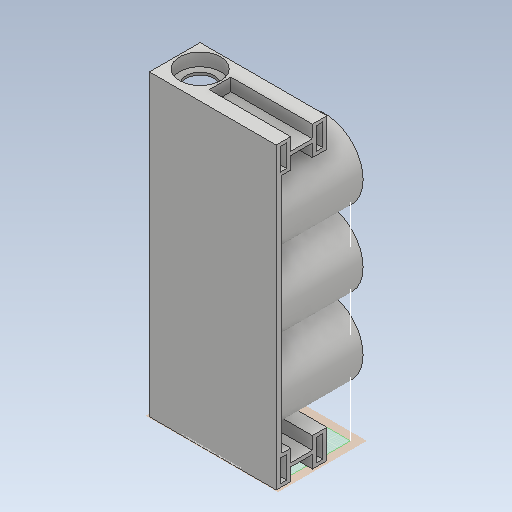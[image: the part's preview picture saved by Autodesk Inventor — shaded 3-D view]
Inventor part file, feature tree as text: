
AUTODESK INVENTOR PART (.ipt)
format: ipt  version: 2020 (Build 240168000, 168)  size: 757,760 bytes
history: native  units: mm
features: sketch x25, extrude x22, fillet x4
ambient origin geometry x8: Origin, YZ Plane, XZ Plane, XY Plane, X Axis, Y Axis, Z Axis, Center Point
bodies: Solid1 (feature_tree)
feature tree (51):
  extrude  "Extrusion1"  Depth=165.0mm
  extrude  "Extrusion2"  Depth=8.5mm
  extrude  "Extrusion3"  Depth=25.0mm TaperAngle=0.0deg
  extrude  "Extrusion4"  Depth=22.75mm
  extrude  "Extrusion5"  Depth=15.5mm
  extrude  "Extrusion6"  Depth=7.1mm TaperAngle=0.0deg
  fillet  "Fillet1"  Radius=5.0mm
  extrude  "Extrusion7"  Depth=10.0mm TaperAngle=0.0deg
  fillet  "Fillet2"  Radius=2.0mm
  extrude  "Extrusion8"  Depth=16.0mm
  extrude  "Extrusion9"  Depth=16.0mm
  fillet  "Fillet3"  Radius=8.0mm
  extrude  "Extrusion10"  Depth=6.0mm
  extrude  "Extrusion11"  Depth=12.25mm
  sketch  "Sketch12"  dims[d32=12.25mm d33=3.5mm]
  sketch  "Sketch13"  dims[d34=12.25mm d35=12.25mm]
  extrude  "Extrusion12"  Depth=12.25mm
  extrude  "Extrusion13"  Depth=12.25mm
  sketch  "Sketch16"  dims[d41=8.0mm d42=1.0mm]
  extrude  "Extrusion14"  Depth=40.0mm TaperAngle=0.0deg
  extrude  "Extrusion15"  Depth=2.0mm
  extrude  "Extrusion16"  Depth=1.0mm
  extrude  "Extrusion17"  Depth=2.0mm TaperAngle=0.0deg
  extrude  "Extrusion18"  Depth=7.1mm TaperAngle=0.0deg
  fillet  "Fillet4"  Radius=3.0mm
  extrude  "Extrusion19"  Depth=42.0mm
  extrude  "Extrusion20"  Depth=42.0mm
  extrude  "Extrusion21"  Depth=42.0mm
  extrude  "Extrusion22"  Depth=2.0mm
  sketch  "Sketch1"  dims[d0=25.0mm d1=165.0mm]
  sketch  "Sketch2"  dims[d2=3.0mm d3=0.0mm d4=8.5mm]
  sketch  "Sketch3"  dims[d5=8.5mm d6=25.0mm d7=0.0mm]
  sketch  "Sketch4"  dims[d8=25.0mm d9=22.75mm]
  sketch  "Sketch5"  dims[d10=7.1mm d11=0.0mm d12=15.5mm]
  sketch  "Sketch6"  dims[d13=165.0mm d14=0.0mm d15=7.1mm d16=0.0mm d17=5.0mm]
  sketch  "Sketch7"  dims[d18=5.0mm d19=10.0mm d20=0.0mm d21=2.0mm]
  sketch  "Sketch8"  dims[d22=16.0mm d23=8.0mm]
  sketch  "Sketch9"  dims[d24=16.0mm d25=16.0mm d26=8.0mm]
  sketch  "Sketch10"  dims[d27=45.0mm d28=0.0mm d29=6.0mm]
  sketch  "Sketch11"  dims[d30=12.25mm d31=3.5mm]
  sketch  "Sketch14"  dims[d36=3.5mm d37=40.0mm d38=0.0mm]
  sketch  "Sketch15"  dims[d39=1.0mm d40=2.0mm]
  sketch  "Sketch17"  dims[d43=2.0mm d44=12.0mm d45=0.0mm]
  sketch  "Sketch18"  dims[d46=6.0mm d47=7.1mm d48=0.0mm d49=3.0mm d50=0.0mm]
  sketch  "Sketch19"  dims[d51=42.0mm d52=38.75mm]
  sketch  "Sketch20"  dims[d53=42.0mm d54=38.75mm]
  sketch  "Sketch21"  dims[d55=42.0mm d56=38.75mm]
  sketch  "Sketch22"  dims[d57=45.0mm d58=0.0mm d59=2.0mm]
  sketch  "Sketch23"  dims[d60=4.0mm]
  sketch  "Sketch24"  dims[d61=2.0mm]
  sketch  "Sketch25"  dims[d62=4.0mm d63=45.0mm d64=0.0mm d65=10.0mm d66=12.0mm d67=0.0mm d68=2.0mm d69=0.0mm d70=2.0mm d71=0.0mm d72=2.0mm d73=2.0mm d74=5.0mm d75=0.0mm d76=2.0mm d77=2.0mm d78=7.0mm d79=0.0mm d80=1.0mm d81=0.25mm d82=0.25mm d83=44.75mm d84=0.0mm d85=44.0mm d86=0.0mm d87=22.6mm d88=8.5mm d89=0.0mm d90=22.6mm d91=8.5mm d92=0.0mm]
